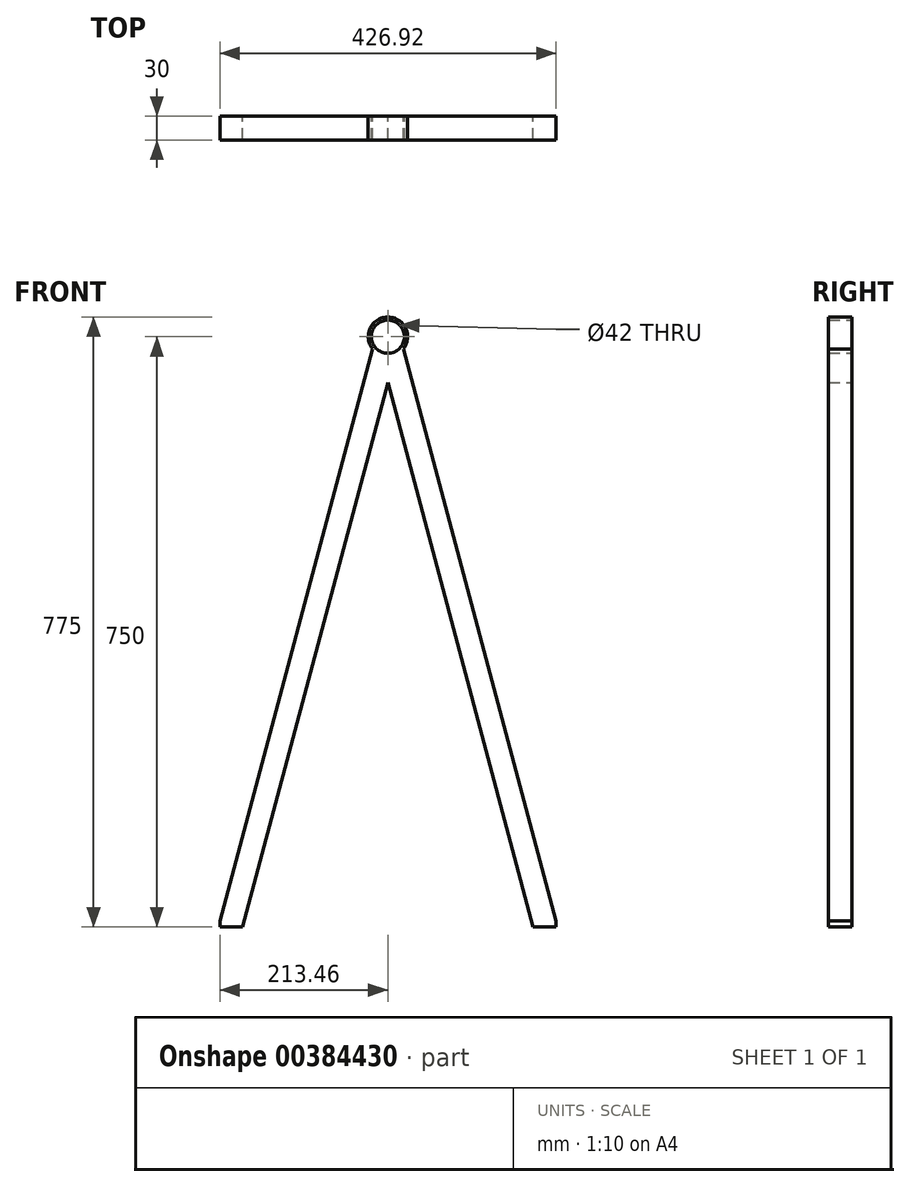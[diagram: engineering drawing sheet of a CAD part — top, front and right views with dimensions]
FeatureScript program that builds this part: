
annotation { "Feature Type Name" : "Feature", "Feature Type Description" : "" }
export const myFeature = defineFeature(function(context is Context, id is Id, definition is map)
    precondition{}
    {
        {
            var Q0;
            Q0=qCreatedBy(makeId("Front.planeOp"),FACE);
            var sketch = newSketch(context, id + "F0", { "sketchPlane" : qUnion([Q0])});
            skLineSegment(sketch, "E0", {"start": v(-250, 0) * mm, "end": v(250, 0) * mm, "construction": true});
            skCircle(sketch, "E1", {"center": v(0, 750) * mm, "radius": 25 * mm, "construction": true});
            skLineSegment(sketch, "E2", {"start": v(-213.46, 7.73) * mm, "end": v(-20.94, 729.7) * mm});
            skLineSegment(sketch, "E3", {"start": v(-20.94, 729.7) * mm, "end": v(8.05, 721.98) * mm, "construction": true});
            skLineSegment(sketch, "E4", {"start": v(8.05, 721.98) * mm, "end": v(-184.48, 0) * mm});
            skLineSegment(sketch, "E5", {"start": v(-184.48, 0) * mm, "end": v(-213.46, 7.73) * mm, "construction": true});
            skLineSegment(sketch, "E6", {"start": v(-200, 0) * mm, "end": v(0, 750) * mm, "construction": true});
            skLineSegment(sketch, "E7", {"start": v(-213.46, 7.73) * mm, "end": v(-213.46, 0) * mm});
            skLineSegment(sketch, "E8", {"start": v(-213.46, 0) * mm, "end": v(-184.48, 0) * mm});
            skLineSegment(sketch, "E9", {"start": v(-20.94, 729.7) * mm, "end": v(-19.65, 734.54) * mm});
            skLineSegment(sketch, "E10", {"start": v(8.05, 721.98) * mm, "end": v(9.34, 726.81) * mm});
            skArc(sketch, "E11", {"start": v(9.34, 726.81) * mm, "mid": v(6.44, 774.16) * mm, "end": v(-19.65, 734.54) * mm});
            skLineSegment(sketch, "E12", {"start": v(0, 0) * mm, "end": v(0, 365) * mm, "construction": true});
            skLineSegment(sketch, "E13.MirrorCS", {"start": v(20.94, 729.7) * mm, "end": v(-8.05, 721.98) * mm, "construction": true});
            skLineSegment(sketch, "E14.MirrorCS", {"start": v(-8.05, 721.98) * mm, "end": v(-9.34, 726.81) * mm});
            skLineSegment(sketch, "E15.MirrorCS", {"start": v(20.94, 729.7) * mm, "end": v(19.65, 734.54) * mm});
            skLineSegment(sketch, "E16.MirrorCS", {"start": v(213.46, 0) * mm, "end": v(184.48, 0) * mm});
            skLineSegment(sketch, "E17.MirrorCS", {"start": v(213.46, 7.73) * mm, "end": v(213.46, 0) * mm});
            skLineSegment(sketch, "E18.MirrorCS", {"start": v(200, 0) * mm, "end": v(0, 750) * mm, "construction": true});
            skLineSegment(sketch, "E19.MirrorCS", {"start": v(184.48, 0) * mm, "end": v(213.46, 7.73) * mm, "construction": true});
            skLineSegment(sketch, "E20.MirrorCS", {"start": v(213.46, 7.73) * mm, "end": v(20.94, 729.7) * mm});
            skLineSegment(sketch, "E21.MirrorCS", {"start": v(-8.05, 721.98) * mm, "end": v(184.48, 0) * mm});
            skArc(sketch, "E22.MirrorCS", {"start": v(-9.34, 726.81) * mm, "mid": v(-6.44, 774.16) * mm, "end": v(19.65, 734.54) * mm});
            skCircle(sketch, "E23", {"center": v(0, 750) * mm, "radius": 21 * mm});
            skSolve(sketch);
        }
        {
            var Q0;
            {var subQ0=sQuery(id+"F0.wireOp",EDGE,"E10");Q0=makeQuery(id+"F0.imprint","IMPRINT",FACE,{"disambiguationData":[TD([[makeQuery(id+"F0.imprint","IMPRINT",EDGE,{"derivedFrom":subQ0}),-1.0]])]});}
            var Q1;
            Q1=makeQuery(id+"F0.imprint","IMPRINT",FACE,{"disambiguationData":[TD([[makeQuery(id+"F0.imprint","IMPRINT",EDGE,{"derivedFrom":sQuery(id+"F0.wireOp",EDGE,"E2")}),-1.0]])]});
            var Q2;
            {var subQ2=sQuery(id+"F0.wireOp",EDGE,"E10");Q2=makeQuery(id+"F0.imprint","IMPRINT",FACE,{"disambiguationData":[TD([[makeQuery(id+"F0.imprint","IMPRINT",EDGE,{"derivedFrom":subQ2}),1.0]])]});}
            extrude(context, id + "F1", {"entities" : qUnion([Q0, Q1, Q2]), "depth" : 30 * mm});
        }
    });
